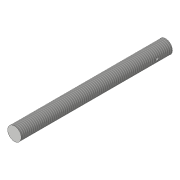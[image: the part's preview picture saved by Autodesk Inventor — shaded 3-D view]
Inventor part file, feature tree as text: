
AUTODESK INVENTOR PART (.ipt)
format: ipt  version: 2019 (Build 230136000, 136)  size: 93,184 bytes
history: native  units: in
note: dims shown in document units (in); Inventor stores cm internally (conversion verified against a paired STEP export)
features: extrude x2, sketch x2, thread x1
ambient origin geometry x8: Origin, YZ Plane, XZ Plane, XY Plane, X Axis, Y Axis, Z Axis, Center Point
bodies: Solid1 (feature_tree)
feature tree (5):
  extrude  "Extrusion1"  Depth=3.937in TaperAngle=0.0deg
  extrude  "Extrusion2"  Depth=0.3937in
  thread  "Thread1"  [1 undecoded]
  sketch  "Sketch1"  dims[d0=0.3543in d1=3.937in d2=0.0in]
  sketch  "Sketch2"  dims[d3=0.0394in d4=0.3937in d5=0.3937in d6=0.0787in d7=0.0in d8=0.0in d9=0.3937in d10=0.0in]
note: 1 required parameter value undecoded (feature->parameter linkage not recoverable at this tier; creation-order binding heuristic only, values carry confidence <= 0.55)
